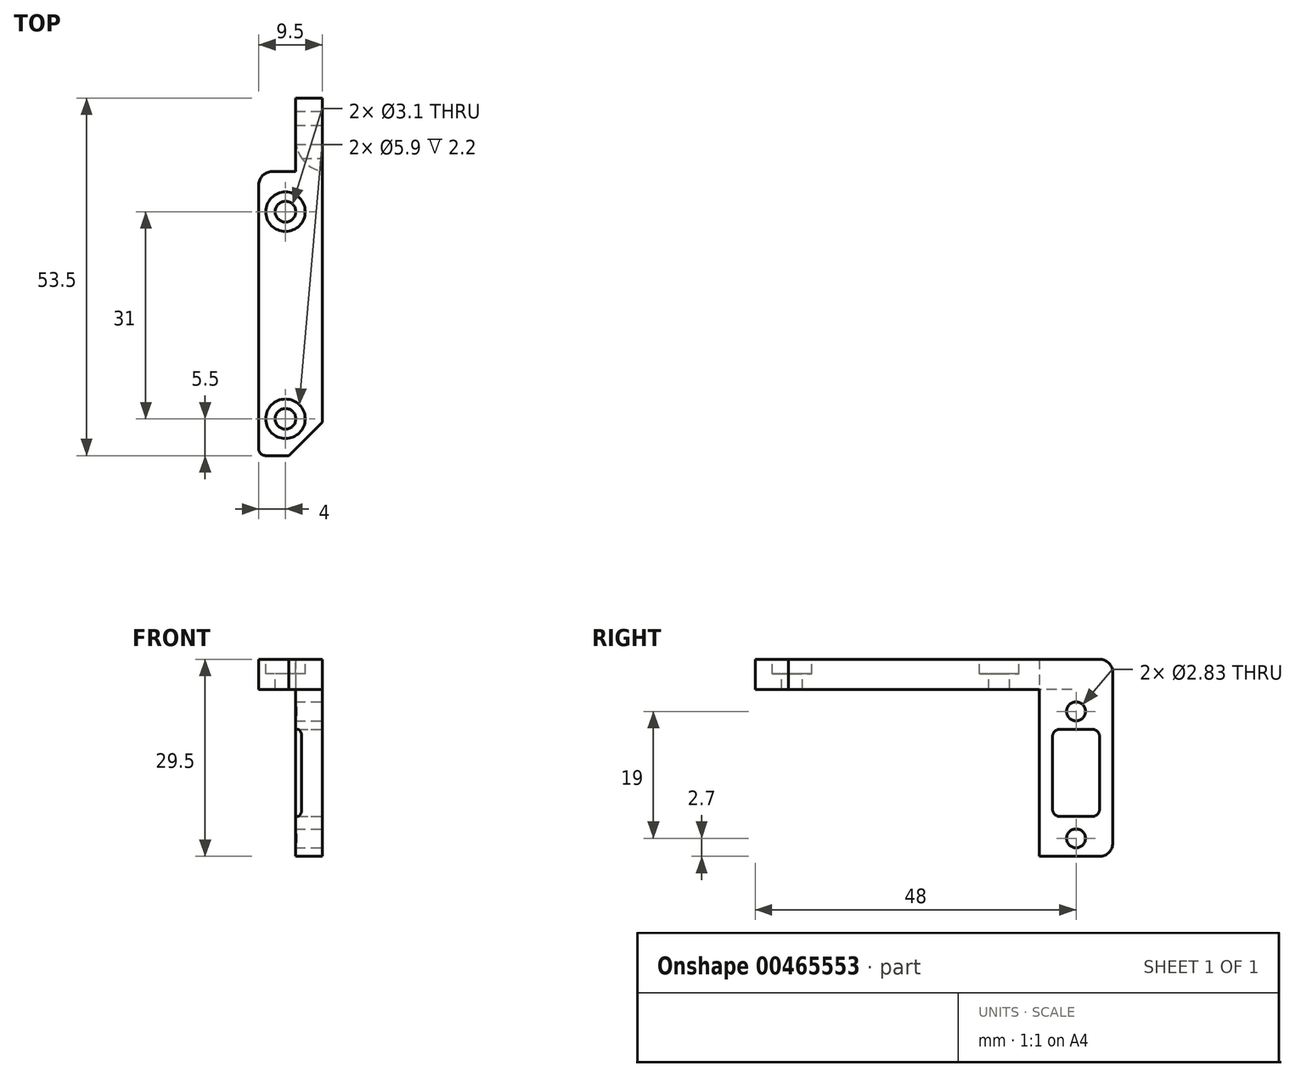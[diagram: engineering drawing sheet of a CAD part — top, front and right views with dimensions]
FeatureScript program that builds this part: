
annotation { "Feature Type Name" : "Feature", "Feature Type Description" : "" }
export const myFeature = defineFeature(function(context is Context, id is Id, definition is map)
    precondition{}
    {
        {
            var Q0;
            Q0=qCreatedBy(makeId("Top.planeOp"),FACE);
            var sketch = newSketch(context, id + "F0", { "sketchPlane" : qUnion([Q0])});
            skLineSegment(sketch, "E0.bottom", {"start": v(0, 0) * mm, "end": v(-9.5, 0) * mm});
            skLineSegment(sketch, "E0.top", {"start": v(0, 42.5) * mm, "end": v(-9.5, 42.5) * mm});
            skLineSegment(sketch, "E0.left", {"start": v(0, 0) * mm, "end": v(0, 42.5) * mm});
            skLineSegment(sketch, "E0.right", {"start": v(-9.5, 0) * mm, "end": v(-9.5, 42.5) * mm});
            skSolve(sketch);
        }
        {
            var Q0;
            Q0 = qSketchRegion(id + "F0", true);
            extrude(context, id + "F1", {"entities" : qUnion([Q0]), "depth" : 4.5 * mm});
        }
        {
            var Q0;
            Q0=makeQuery(id+"F1.opExtrude","CAP_FACE",FACE,{"disambiguationData":[OSD([sQuery(id+"F0.wireOp",EDGE,"E0.bottom"),sQuery(id+"F0.wireOp",EDGE,"E0.top"),sQuery(id+"F0.wireOp",EDGE,"E0.left"),sQuery(id+"F0.wireOp",EDGE,"E0.right")])],"isStart":false});
            var sketch = newSketch(context, id + "F2", { "sketchPlane" : qUnion([Q0])});
            skPoint(sketch, "E1", {"position": v(-5.5, 5.5) * mm});
            skPoint(sketch, "E2", {"position": v(-5.5, 36.5) * mm});
            skSolve(sketch);
        }
        {
            var Q0;
            Q0=sQuery(id+"F2.wireOp",VERTEX,"E2");
            var Q1;
            Q1=sQuery(id+"F2.wireOp",VERTEX,"E1");
            var Q2;
            Q2=makeQuery(id+"F1.opExtrude","SWEPT_BODY",BODY,{"disambiguationData":[OSD([sQuery(id+"F0.wireOp",EDGE,"E0.bottom"),sQuery(id+"F0.wireOp",EDGE,"E0.top"),sQuery(id+"F0.wireOp",EDGE,"E0.left"),sQuery(id+"F0.wireOp",EDGE,"E0.right")])]});
            hole(context, id + "F3", {"style" : HoleStyle.C_BORE, "endStyle" : HoleEndStyle.THROUGH, "holeDiameter" : 3.1 * mm, "cBoreDiameter" : 5.9 * mm, "cBoreDepth" : 2.2 * mm, "tappedDepth" : 12 * mm, "tapClearance" : 3, "locations" : qUnion([Q0, Q1]), "scope" : qUnion([Q2])});
        }
        {
            var Q0;
            Q0=qCreatedBy(makeId("Right.planeOp"),FACE);
            var sketch = newSketch(context, id + "F4", { "sketchPlane" : qUnion([Q0])});
            skLineSegment(sketch, "E3.bottom", {"start": v(42.5, 4.5) * mm, "end": v(53.5, 4.5) * mm});
            skLineSegment(sketch, "E3.top", {"start": v(42.5, -25) * mm, "end": v(53.5, -25) * mm});
            skLineSegment(sketch, "E3.left", {"start": v(42.5, 4.5) * mm, "end": v(42.5, -25) * mm});
            skLineSegment(sketch, "E3.right", {"start": v(53.5, 4.5) * mm, "end": v(53.5, -25) * mm});
            skSolve(sketch);
        }
        {
            var Q0;
            Q0 = qSketchRegion(id + "F4", true);
            extrude(context, id + "F5", {"entities" : qUnion([Q0]), "operationType" : NewBodyOperationType.ADD, "oppositeDirection" : true, "depth" : 4 * mm});
        }
        {
            var Q0;
            Q0=makeQuery(id+"F5.boolean.opBoolean","MERGE",FACE,{"derivedFrom":[makeQuery(id+"F1.opExtrude","SWEPT_FACE",FACE,{"disambiguationData":[OSD([sQuery(id+"F0.wireOp",EDGE,"E0.left")])]}),makeQuery(id+"F5.opExtrude","CAP_FACE",FACE,{"disambiguationData":[OSD([sQuery(id+"F4.wireOp",EDGE,"E3.bottom"),sQuery(id+"F4.wireOp",EDGE,"E3.top"),sQuery(id+"F4.wireOp",EDGE,"E3.left"),sQuery(id+"F4.wireOp",EDGE,"E3.right")])],"isStart":true})]});
            var sketch = newSketch(context, id + "F6", { "sketchPlane" : qUnion([Q0])});
            skPoint(sketch, "E4", {"position": v(48, -3.3) * mm});
            skPoint(sketch, "E5", {"position": v(48, -22.3) * mm});
            skSolve(sketch);
        }
        {
            var Q0;
            Q0=sQuery(id+"F6.wireOp",VERTEX,"E4");
            var Q1;
            Q1=sQuery(id+"F6.wireOp",VERTEX,"E5");
            var Q2;
            Q2=makeQuery(id+"F1.opExtrude","SWEPT_BODY",BODY,{"disambiguationData":[OSD([sQuery(id+"F0.wireOp",EDGE,"E0.bottom"),sQuery(id+"F0.wireOp",EDGE,"E0.top"),sQuery(id+"F0.wireOp",EDGE,"E0.left"),sQuery(id+"F0.wireOp",EDGE,"E0.right")])]});
            hole(context, id + "F7", {"style" : HoleStyle.SIMPLE, "endStyle" : HoleEndStyle.THROUGH, "holeDiameter" : 2.83 * mm, "tappedDepth" : 12 * mm, "tapClearance" : 3, "locations" : qUnion([Q0, Q1]), "scope" : qUnion([Q2])});
        }
        {
            var Q0;
            Q0=makeQuery(id+"F5.boolean.opBoolean","MERGE",FACE,{"derivedFrom":[makeQuery(id+"F1.opExtrude","SWEPT_FACE",FACE,{"disambiguationData":[OSD([sQuery(id+"F0.wireOp",EDGE,"E0.left")])]}),makeQuery(id+"F5.opExtrude","CAP_FACE",FACE,{"disambiguationData":[OSD([sQuery(id+"F4.wireOp",EDGE,"E3.bottom"),sQuery(id+"F4.wireOp",EDGE,"E3.top"),sQuery(id+"F4.wireOp",EDGE,"E3.left"),sQuery(id+"F4.wireOp",EDGE,"E3.right")])],"isStart":true})]});
            var sketch = newSketch(context, id + "F8", { "sketchPlane" : qUnion([Q0])});
            skLineSegment(sketch, "E6.bottom", {"start": v(44.5, -6) * mm, "end": v(51.5, -6) * mm});
            skLineSegment(sketch, "E6.top", {"start": v(44.5, -19) * mm, "end": v(51.5, -19) * mm});
            skLineSegment(sketch, "E6.left", {"start": v(44.5, -6) * mm, "end": v(44.5, -19) * mm});
            skLineSegment(sketch, "E6.right", {"start": v(51.5, -6) * mm, "end": v(51.5, -19) * mm});
            skSolve(sketch);
        }
        {
            var Q0;
            Q0=makeQuery(id+"F8.imprint","IMPRINT",FACE,{"disambiguationData":[TD([[makeQuery(id+"F8.imprint","IMPRINT",EDGE,{"derivedFrom":sQuery(id+"F8.wireOp",EDGE,"E6.bottom")}),-1.0]])]});
            extrude(context, id + "F9", {"entities" : qUnion([Q0]), "operationType" : NewBodyOperationType.REMOVE, "oppositeDirection" : true, "depth" : 25 * mm});
        }
        {
            var Q0;
            {var subQ0=sQuery(id+"F4.wireOp",EDGE,"E3.left");Q0=makeQuery(id+"F5.boolean.opBoolean","SPLIT",EDGE,{"disambiguationData":[topologyDisambiguationEdgeConnected([makeQuery(id+"F1.opExtrude","SWEPT_FACE",FACE,{"disambiguationData":[OSD([sQuery(id+"F0.wireOp",EDGE,"E0.top")])]})])],"derivedFrom":makeQuery(id+"F5.opExtrude","CAP_EDGE",EDGE,{"disambiguationData":[OSD([subQ0])],"isStart":false})});}
            fillet(context, id + "F10", {"entities" : qUnion([Q0]), "radius" : 5 * mm, "tangentPropagation" : true, "allowEdgeOverflow" : false});
        }
        {
            var Q0;
            Q0=makeQuery(id+"F5.opExtrude","SWEPT_EDGE",EDGE,{"disambiguationData":[OSD([sQuery(id+"F4.wireOp",EDGE,"E3.bottom"),sQuery(id+"F4.wireOp",EDGE,"E3.right")])]});
            var Q1;
            Q1=makeQuery(id+"F5.opExtrude","SWEPT_EDGE",EDGE,{"disambiguationData":[OSD([sQuery(id+"F4.wireOp",EDGE,"E3.top"),sQuery(id+"F4.wireOp",EDGE,"E3.right")])]});
            var Q2;
            Q2=makeQuery(id+"F5.opExtrude","SWEPT_EDGE",EDGE,{"disambiguationData":[OSD([sQuery(id+"F4.wireOp",EDGE,"E3.top"),sQuery(id+"F4.wireOp",EDGE,"E3.left")])]});
            var Q3;
            Q3=makeQuery(id+"F1.opExtrude","SWEPT_EDGE",EDGE,{"disambiguationData":[OSD([sQuery(id+"F0.wireOp",EDGE,"E0.top"),sQuery(id+"F0.wireOp",EDGE,"E0.right")])]});
            fillet(context, id + "F11", {"entities" : qUnion([Q0, Q1, Q2, Q3]), "radius" : 2 * mm, "tangentPropagation" : true, "allowEdgeOverflow" : false});
        }
        {
            var Q0;
            Q0=makeQuery(id+"F1.opExtrude","SWEPT_EDGE",EDGE,{"disambiguationData":[OSD([sQuery(id+"F0.wireOp",EDGE,"E0.bottom"),sQuery(id+"F0.wireOp",EDGE,"E0.left")])]});
            chamfer(context, id + "F12", {"entities" : qUnion([Q0]), "width" : 5 * mm, "tangentPropagation" : true});
        }
        {
            var Q0;
            Q0=makeQuery(id+"F9.boolean.opBoolean","COPY",EDGE,{"derivedFrom":makeQuery(id+"F9.opExtrude","SWEPT_EDGE",EDGE,{"disambiguationData":[OSD([sQuery(id+"F8.wireOp",EDGE,"E6.bottom"),sQuery(id+"F8.wireOp",EDGE,"E6.left")])]})});
            var Q1;
            Q1=makeQuery(id+"F9.boolean.opBoolean","COPY",EDGE,{"derivedFrom":makeQuery(id+"F9.opExtrude","SWEPT_EDGE",EDGE,{"disambiguationData":[OSD([sQuery(id+"F8.wireOp",EDGE,"E6.bottom"),sQuery(id+"F8.wireOp",EDGE,"E6.right")])]})});
            var Q2;
            Q2=makeQuery(id+"F9.boolean.opBoolean","COPY",EDGE,{"derivedFrom":makeQuery(id+"F9.opExtrude","SWEPT_EDGE",EDGE,{"disambiguationData":[OSD([sQuery(id+"F8.wireOp",EDGE,"E6.top"),sQuery(id+"F8.wireOp",EDGE,"E6.left")])]})});
            var Q3;
            Q3=makeQuery(id+"F9.boolean.opBoolean","COPY",EDGE,{"derivedFrom":makeQuery(id+"F9.opExtrude","SWEPT_EDGE",EDGE,{"disambiguationData":[OSD([sQuery(id+"F8.wireOp",EDGE,"E6.top"),sQuery(id+"F8.wireOp",EDGE,"E6.right")])]})});
            var Q4;
            Q4=makeQuery(id+"F1.opExtrude","SWEPT_EDGE",EDGE,{"disambiguationData":[OSD([sQuery(id+"F0.wireOp",EDGE,"E0.bottom"),sQuery(id+"F0.wireOp",EDGE,"E0.right")])]});
            fillet(context, id + "F13", {"entities" : qUnion([Q0, Q1, Q2, Q3, Q4]), "radius" : 1 * mm, "tangentPropagation" : true, "allowEdgeOverflow" : false});
        }
    });
